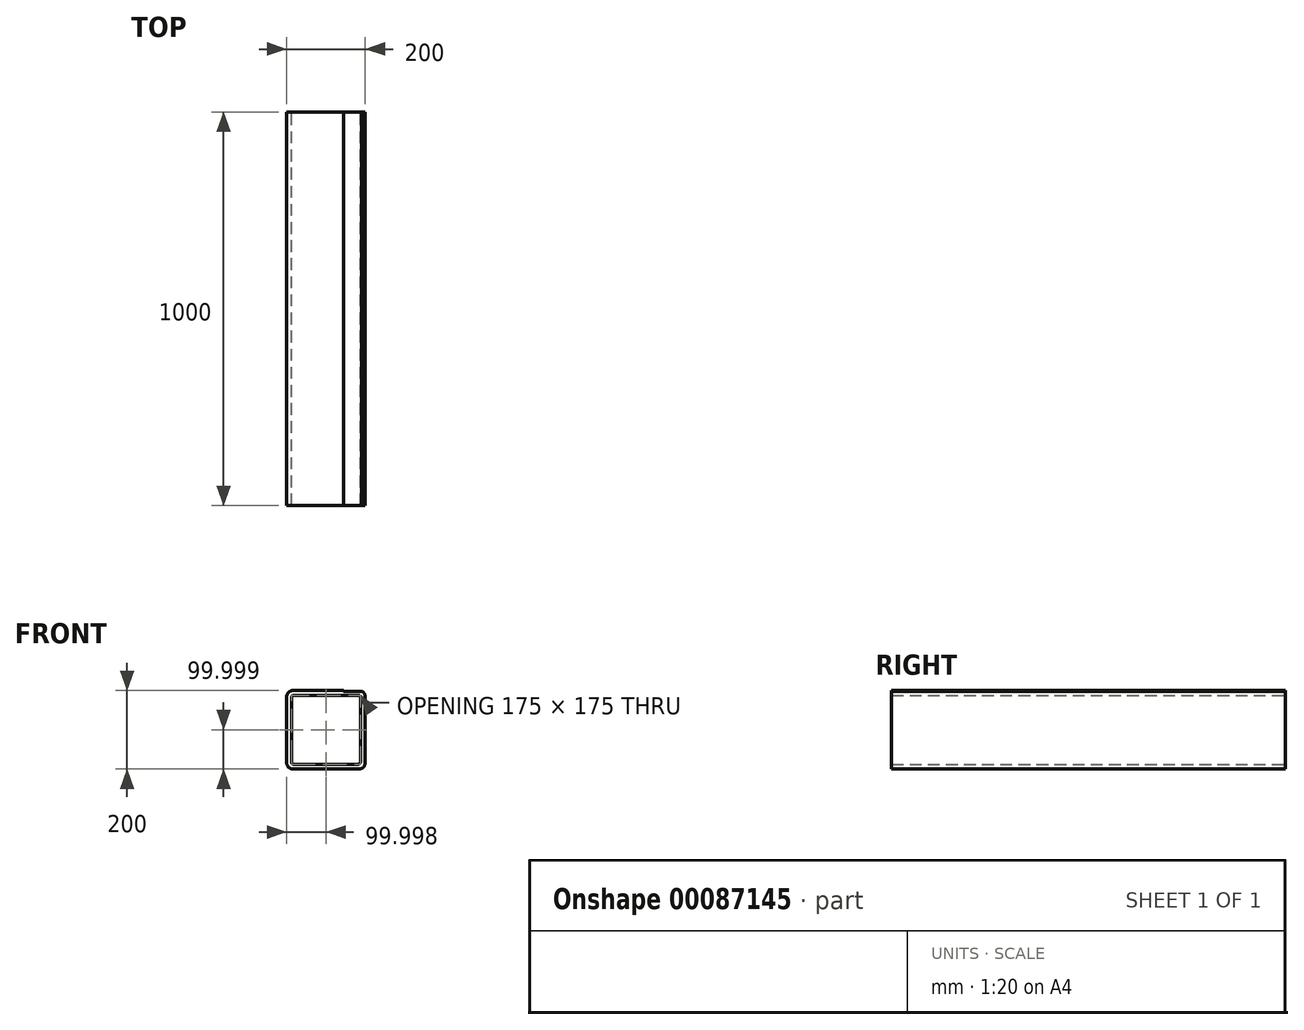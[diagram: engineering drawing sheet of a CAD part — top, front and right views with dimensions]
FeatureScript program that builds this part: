
annotation { "Feature Type Name" : "Feature", "Feature Type Description" : "" }
export const myFeature = defineFeature(function(context is Context, id is Id, definition is map)
    precondition{}
    {
        {
            var Q0;
            Q0=qCreatedBy(makeId("Front.planeOp"),FACE);
            var sketch = newSketch(context, id + "F0", { "sketchPlane" : qUnion([Q0])});
            skLineSegment(sketch, "E0.top", {"start": v(-102.1, -99.2) * mm, "end": v(97.9, -99.2) * mm});
            skLineSegment(sketch, "E0.left", {"start": v(-102.1, 100.8) * mm, "end": v(-102.1, -99.2) * mm});
            skLineSegment(sketch, "E0.right", {"start": v(97.9, 100.8) * mm, "end": v(97.9, -99.2) * mm});
            skLineSegment(sketch, "E1.top", {"start": v(-89.6, -86.7) * mm, "end": v(85.4, -86.7) * mm});
            skLineSegment(sketch, "E1.left", {"start": v(-89.6, 88.3) * mm, "end": v(-89.6, -86.7) * mm});
            skLineSegment(sketch, "E1.right", {"start": v(85.4, 88.3) * mm, "end": v(85.4, -86.7) * mm});
            skLineSegment(sketch, "E2.right", {"start": v(-102.1, -11.22) * mm, "end": v(-102.1, -11.64) * mm});
            skLineSegment(sketch, "E3", {"start": v(-102.1, 100.8) * mm, "end": v(97.9, 100.8) * mm});
            skLineSegment(sketch, "E4", {"start": v(-89.6, 88.3) * mm, "end": v(85.4, 88.3) * mm});
            skSolve(sketch);
        }
        {
            var Q0;
            {var subQ1=sQuery(id+"F0.wireOp",EDGE,"E0.top");Q0=makeQuery(id+"F0.imprint","IMPRINT",FACE,{"disambiguationData":[TD([[makeQuery(id+"F0.imprint","IMPRINT",EDGE,{"derivedFrom":subQ1}),1.0]])]});}
            extrude(context, id + "F1", {"entities" : qUnion([Q0]), "endBound" : BoundingType.SYMMETRIC, "depth" : 1000 * mm});
        }
        {
            var Q0;
            Q0=makeQuery(id+"F1.opExtrude","SWEPT_EDGE",EDGE,{"disambiguationData":[OSD([sQuery(id+"F0.wireOp",EDGE,"E1.top"),sQuery(id+"F0.wireOp",EDGE,"E1.left")])]});
            var Q1;
            Q1=makeQuery(id+"F1.opExtrude","SWEPT_EDGE",EDGE,{"disambiguationData":[OSD([sQuery(id+"F0.wireOp",EDGE,"E1.left"),sQuery(id+"F0.wireOp",EDGE,"E4")])]});
            var Q2;
            Q2=makeQuery(id+"F1.opExtrude","SWEPT_EDGE",EDGE,{"disambiguationData":[OSD([sQuery(id+"F0.wireOp",EDGE,"E1.right"),sQuery(id+"F0.wireOp",EDGE,"E4")])]});
            var Q3;
            Q3=makeQuery(id+"F1.opExtrude","SWEPT_EDGE",EDGE,{"disambiguationData":[OSD([sQuery(id+"F0.wireOp",EDGE,"E1.top"),sQuery(id+"F0.wireOp",EDGE,"E1.right")])]});
            fillet(context, id + "F2", {"entities" : qUnion([Q0, Q1, Q2, Q3]), "radius" : 5 * mm, "tangentPropagation" : true, "allowEdgeOverflow" : false});
        }
        {
            var Q0;
            Q0=makeQuery(id+"F1.opExtrude","SWEPT_EDGE",EDGE,{"disambiguationData":[OSD([sQuery(id+"F0.wireOp",EDGE,"E0.right"),sQuery(id+"F0.wireOp",EDGE,"E3")])]});
            var Q1;
            Q1=makeQuery(id+"F1.opExtrude","SWEPT_EDGE",EDGE,{"disambiguationData":[OSD([sQuery(id+"F0.wireOp",EDGE,"E0.left"),sQuery(id+"F0.wireOp",EDGE,"E3")])]});
            var Q2;
            Q2=makeQuery(id+"F1.opExtrude","SWEPT_EDGE",EDGE,{"disambiguationData":[OSD([sQuery(id+"F0.wireOp",EDGE,"E0.top"),sQuery(id+"F0.wireOp",EDGE,"E0.left")])]});
            var Q3;
            Q3=makeQuery(id+"F1.opExtrude","SWEPT_EDGE",EDGE,{"disambiguationData":[OSD([sQuery(id+"F0.wireOp",EDGE,"E0.top"),sQuery(id+"F0.wireOp",EDGE,"E0.right")])]});
            fillet(context, id + "F3", {"entities" : qUnion([Q0, Q1, Q2, Q3]), "radius" : 17 * mm, "tangentPropagation" : true, "allowEdgeOverflow" : false});
        }
        {
            var Q0;
            Q0=makeQuery(id+"F1.opExtrude","CAP_FACE",FACE,{"disambiguationData":[OSD([sQuery(id+"F0.wireOp",EDGE,"E0.top"),sQuery(id+"F0.wireOp",EDGE,"E0.left"),sQuery(id+"F0.wireOp",EDGE,"E0.right"),sQuery(id+"F0.wireOp",EDGE,"E1.top"),sQuery(id+"F0.wireOp",EDGE,"E1.left"),sQuery(id+"F0.wireOp",EDGE,"E1.right"),sQuery(id+"F0.wireOp",EDGE,"E2.right"),sQuery(id+"F0.wireOp",EDGE,"E3"),sQuery(id+"F0.wireOp",EDGE,"E4")])],"isStart":false});
            var sketch = newSketch(context, id + "F4", { "sketchPlane" : qUnion([Q0])});
            skLineSegment(sketch, "E5.bottom", {"start": v(42.8, 100.8) * mm, "end": v(97.33, 100.8) * mm});
            skLineSegment(sketch, "E5.top", {"start": v(42.8, 98.8) * mm, "end": v(97.33, 98.8) * mm});
            skLineSegment(sketch, "E5.left", {"start": v(42.8, 100.8) * mm, "end": v(42.8, 98.8) * mm});
            skLineSegment(sketch, "E5.right", {"start": v(97.33, 100.8) * mm, "end": v(97.33, 98.8) * mm});
            skSolve(sketch);
        }
        {
            var Q0;
            Q0 = qSketchRegion(id + "F4", true);
            var Q1;
            Q1=makeQuery(id+"F1.opExtrude","CAP_FACE",FACE,{"disambiguationData":[OSD([sQuery(id+"F0.wireOp",EDGE,"E0.top"),sQuery(id+"F0.wireOp",EDGE,"E0.left"),sQuery(id+"F0.wireOp",EDGE,"E0.right"),sQuery(id+"F0.wireOp",EDGE,"E1.top"),sQuery(id+"F0.wireOp",EDGE,"E1.left"),sQuery(id+"F0.wireOp",EDGE,"E1.right"),sQuery(id+"F0.wireOp",EDGE,"E2.right"),sQuery(id+"F0.wireOp",EDGE,"E3"),sQuery(id+"F0.wireOp",EDGE,"E4")])],"isStart":true});
            extrude(context, id + "F5", {"entities" : qUnion([Q0]), "operationType" : NewBodyOperationType.REMOVE, "endBound" : BoundingType.UP_TO_SURFACE, "oppositeDirection" : true, "endBoundEntityFace" : qUnion([Q1]), "depth" : 25 * mm});
        }
    });
